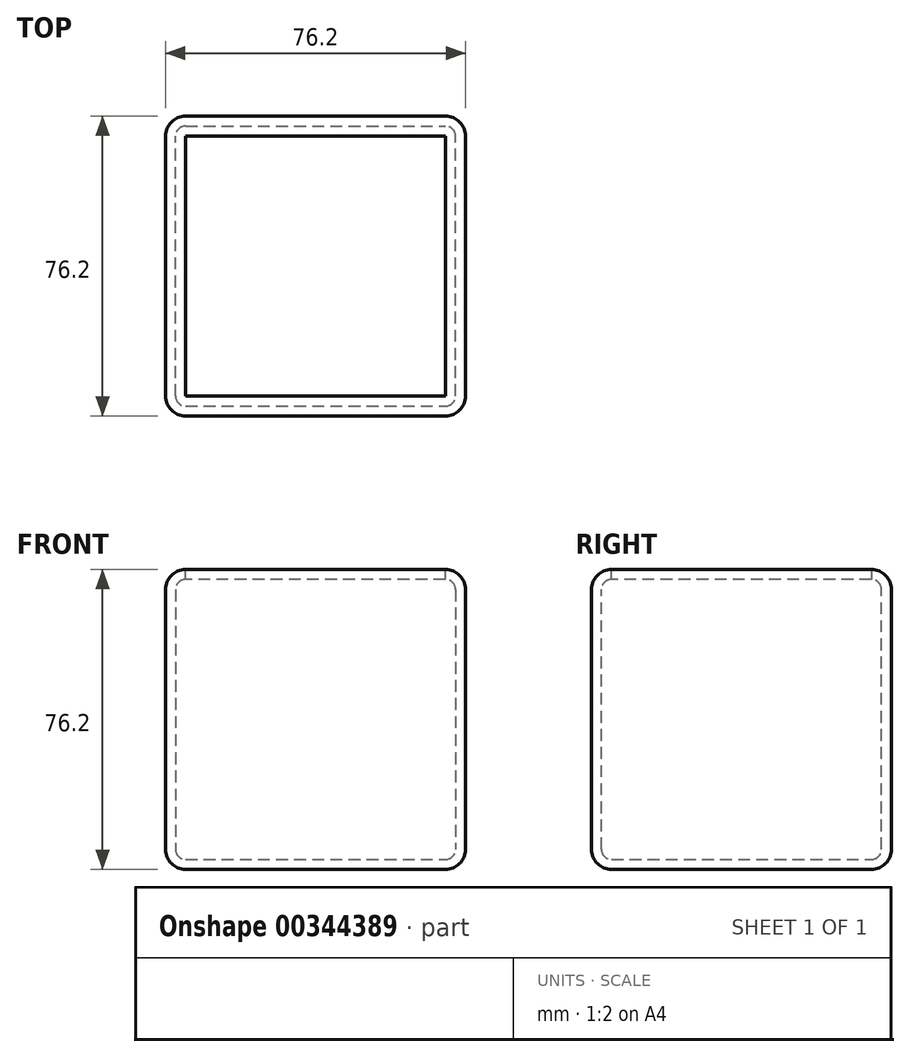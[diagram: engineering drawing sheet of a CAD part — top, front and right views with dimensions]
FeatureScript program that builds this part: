
annotation { "Feature Type Name" : "Feature", "Feature Type Description" : "" }
export const myFeature = defineFeature(function(context is Context, id is Id, definition is map)
    precondition{}
    {
        {
            var Q0;
            Q0=qCreatedBy(makeId("Front.planeOp"),FACE);
            var sketch = newSketch(context, id + "F0", { "sketchPlane" : qUnion([Q0])});
            skLineSegment(sketch, "E0.bottom", {"start": v(-38.1, 38.1) * mm, "end": v(38.1, 38.1) * mm});
            skLineSegment(sketch, "E0.top", {"start": v(-38.1, -38.1) * mm, "end": v(38.1, -38.1) * mm});
            skLineSegment(sketch, "E0.left", {"start": v(-38.1, 38.1) * mm, "end": v(-38.1, -38.1) * mm});
            skLineSegment(sketch, "E0.right", {"start": v(38.1, 38.1) * mm, "end": v(38.1, -38.1) * mm});
            skSolve(sketch);
        }
        {
            var Q0;
            Q0=makeQuery(id+"F0.imprint","IMPRINT",FACE,{"disambiguationData":[TD([[makeQuery(id+"F0.imprint","IMPRINT",EDGE,{"derivedFrom":sQuery(id+"F0.wireOp",EDGE,"E0.bottom")}),-1.0]])]});
            extrude(context, id + "F1", {"entities" : qUnion([Q0]), "endBound" : BoundingType.SYMMETRIC, "depth" : 76.2 * mm});
        }
        {
            var Q0;
            Q0=makeQuery(id+"F1.opExtrude","SWEPT_FACE",FACE,{"disambiguationData":[OSD([sQuery(id+"F0.wireOp",EDGE,"E0.bottom")])]});
            var Q1;
            Q1=makeQuery(id+"F1.opExtrude","SWEPT_FACE",FACE,{"disambiguationData":[OSD([sQuery(id+"F0.wireOp",EDGE,"E0.right")])]});
            var Q2;
            Q2=makeQuery(id+"F1.opExtrude","CAP_FACE",FACE,{"disambiguationData":[OSD([sQuery(id+"F0.wireOp",EDGE,"E0.bottom"),sQuery(id+"F0.wireOp",EDGE,"E0.top"),sQuery(id+"F0.wireOp",EDGE,"E0.left"),sQuery(id+"F0.wireOp",EDGE,"E0.right")])],"isStart":false});
            var Q3;
            Q3=makeQuery(id+"F1.opExtrude","SWEPT_FACE",FACE,{"disambiguationData":[OSD([sQuery(id+"F0.wireOp",EDGE,"E0.top")])]});
            var Q4;
            Q4=makeQuery(id+"F1.opExtrude","SWEPT_FACE",FACE,{"disambiguationData":[OSD([sQuery(id+"F0.wireOp",EDGE,"E0.left")])]});
            var Q5;
            Q5=makeQuery(id+"F1.opExtrude","CAP_FACE",FACE,{"disambiguationData":[OSD([sQuery(id+"F0.wireOp",EDGE,"E0.bottom"),sQuery(id+"F0.wireOp",EDGE,"E0.top"),sQuery(id+"F0.wireOp",EDGE,"E0.left"),sQuery(id+"F0.wireOp",EDGE,"E0.right")])],"isStart":true});
            fillet(context, id + "F2", {"entities" : qUnion([Q0, Q1, Q2, Q3, Q4, Q5]), "radius" : 5.08 * mm, "tangentPropagation" : true, "allowEdgeOverflow" : false});
        }
        {
            var Q0;
            Q0=makeQuery(id+"F1.opExtrude","SWEPT_FACE",FACE,{"disambiguationData":[OSD([sQuery(id+"F0.wireOp",EDGE,"E0.bottom")])]});
            shell(context, id + "F3", {"entities" : qUnion([Q0]), "thickness" : 2.54 * mm});
        }
    });
